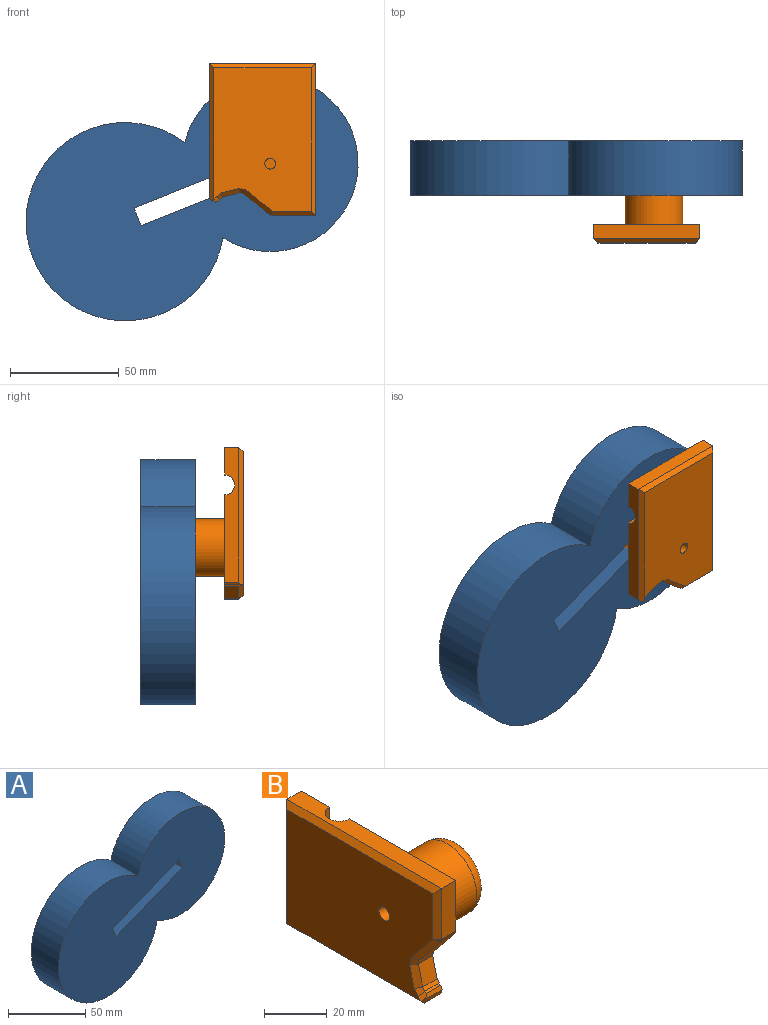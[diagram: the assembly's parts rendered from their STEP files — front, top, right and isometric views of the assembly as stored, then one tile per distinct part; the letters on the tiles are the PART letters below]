
ASSEMBLY  parts=2 mates=1
PART A: 8 faces, bbox 152.5x25x112.6 mm
  f0: cylinder r=40.4mm len=80.79mm, axis (0,1,0), area 5086.7mm2, adj f1,f2,f3
  f1: cylinder r=45.53mm len=91.05mm, axis (0,1,0), area 5912.1mm2, adj f0,f2,f3
  f2: plane 152.53x112.59mm, normal (0,-1,0), area 10610mm2, adj f0,f1,f4,f5,f6,f7
  f3: plane 152.53x112.59mm, normal (0,1,0), area 10610mm2, adj f0,f1,f4,f5,f6,f7
  f4: plane 60.9x25mm, normal (0.37,0,-0.93), area 1640.1mm2, adj f2,f3,f5,f6
  f5: plane 25x8.13mm, normal (-0.93,0,-0.37), area 218.9mm2, adj f2,f3,f4,f7
  f6: plane 25x8.13mm, normal (0.93,0,0.37), area 218.9mm2, adj f2,f3,f4,f7
  f7: plane 60.9x25mm, normal (-0.37,0,0.93), area 1640.1mm2, adj f2,f3,f5,f6
PART B: 35 faces, bbox 33.5x70x48.7 mm
  f0: plane 48.71x48.14mm, normal (1,0,0), area 1594.9mm2, adj f1,f3,f5,f7,f13,f14,f15,f16
  f1: plane 70x6.46mm, normal (0,0,1), area 419.3mm2, adj f0,f3,f4,f6,f26,f34
  f2: plane 66x44.71mm, normal (-1,0,0), area 2737.6mm2, adj f10,f18,f20,f21,f23,f24,f25,f26
  f3: plane 19.91x6.46mm, normal (0,-1,0), area 128.5mm2, adj f0,f1,f28,f30
  f4: plane 48.71x12.74mm, normal (1,0,0), area 620.8mm2, adj f1,f5,f6,f34
  f5: plane 61.95x6.46mm, normal (0,0,-1), area 367.3mm2, adj f0,f4,f6,f21,f31,f34
  f6: plane 48.71x6.46mm, normal (0,1,0), area 314.5mm2, adj f1,f4,f5,f24
  f7: cylinder r=13.24mm len=26.47mm, axis (-1,0,0), area 1663.2mm2, adj f0,f33
  f8: plane 16.47x16.47mm, normal (1,0,0), area 213.1mm2, adj f33
  f9: plane 10x10mm, normal (-1,0,0), area 78.5mm2, adj f12
  f10: cylinder r=2.5mm len=5mm, axis (1,0,0), area 54.3mm2, adj f2,f11
  f11: plane 10x10mm, normal (1,0,0), area 58.9mm2, adj f10,f12
  f12: cylinder r=5mm len=10mm, axis (1,0,0), area 157.1mm2, adj f9,f11
  f13: plane 8.04x6.46mm, normal (0,-0.97,0.25), area 53.6mm2, adj f0,f17,f22,f23
  f14: plane 11.81x9.71mm, normal (0,-0.77,-0.64), area 98.7mm2, adj f0,f22,f27,f30
  f15: plane 6.46x0.77mm, normal (0,-0.52,0.85), area 5.8mm2, adj f0,f17,f18,f32
  f16: plane 6.46x1.78mm, normal (0,-0.96,-0.27), area 11.9mm2, adj f0,f19,f31,f32
  f17: plane 6.46x1.21mm, normal (0,-0.81,0.59), area 9.7mm2, adj f0,f13,f15,f20
  f18: plane 2.7x2.27mm, normal (-0.71,-0.37,0.6), area 4.8mm2, adj f2,f15,f19,f20,f32
  f19: plane 2.3x2mm, normal (-0.26,-0.93,-0.26), area 3.2mm2, adj f16,f18,f21,f31,f32
  f20: plane 2.91x2.83mm, normal (-0.68,-0.59,0.43), area 6.1mm2, adj f2,f17,f18,f23
  f21: plane 62.95x2mm, normal (-0.71,0,-0.71), area 174.7mm2, adj f2,f5,f19,f24,f31
  f22: plane 6.46x1.76mm, normal (0,-0.98,-0.22), area 11.7mm2, adj f0,f13,f14,f25
  f23: plane 8.54x3.99mm, normal (-0.71,-0.69,0.17), area 23.5mm2, adj f2,f13,f20,f25
  f24: plane 48.71x2mm, normal (-0.71,0.71,0), area 132.1mm2, adj f2,f6,f21,f26
  f25: plane 3.53x2.33mm, normal (-0.67,-0.73,-0.16), area 7.3mm2, adj f2,f22,f23,f27
  f26: plane 70x2mm, normal (-0.71,0,0.71), area 192.3mm2, adj f1,f2,f24,f28
  f27: plane 13.08x11.26mm, normal (-0.71,-0.55,-0.45), area 43.3mm2, adj f2,f14,f25,f29
  f28: plane 19.91x2mm, normal (-0.71,-0.71,0), area 53.5mm2, adj f2,f3,f26,f29
  f29: plane 2x2mm, normal (-0.69,-0.69,-0.25), area 1.9mm2, adj f27,f28,f30
  f30: plane 6.46x1.27mm, normal (0,-0.94,-0.34), area 8.7mm2, adj f0,f3,f14,f29
  f31: plane 7.21x1.27mm, normal (0,-0.6,-0.8), area 10.9mm2, adj f0,f5,f16,f19,f21
  f32: plane 7.21x1.49mm, normal (0,-0.93,0.36), area 10.9mm2, adj f0,f15,f16,f18,f19
  f33: torus R=8.24mm, axis (1,0,0), area 563.5mm2, adj f7,f8
  f34: cylinder r=4.56mm len=48.71mm, axis (0,0,-1), area 697.1mm2, adj f0,f1,f4,f5
PLACE A t=(33.29,15.79,3.31)mm
PLACE B rot(axis=(0.58,0.58,0.58),120deg) t=(3.4,-12.96,47.01)mm
MATE revolute B.f7 <-> A.f0  axis (0,1,0) through (38.84,2.29,25.93)mm
